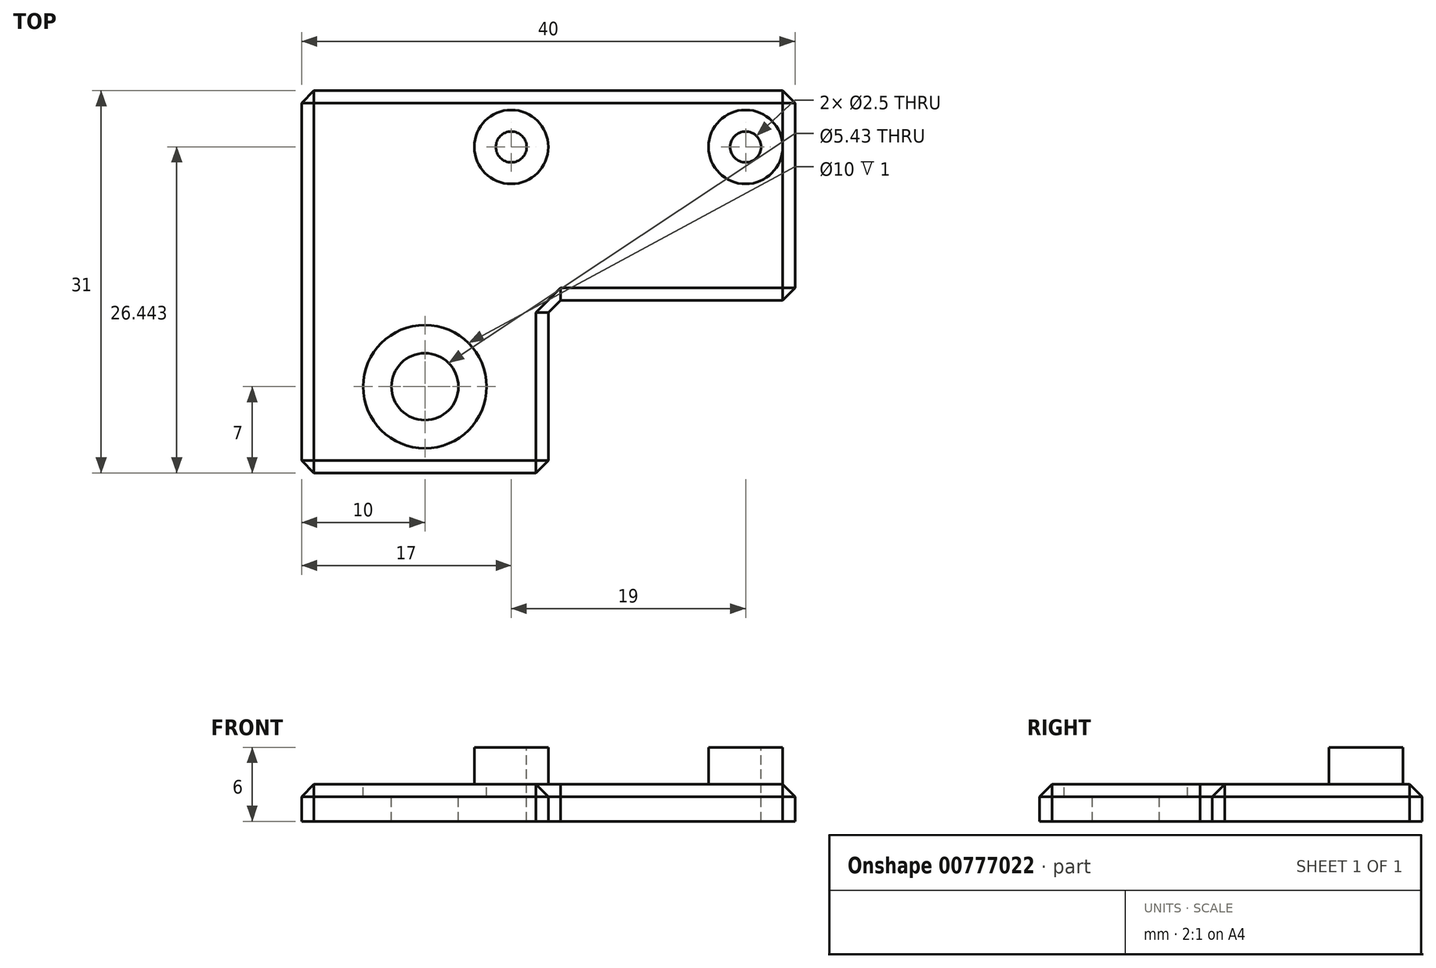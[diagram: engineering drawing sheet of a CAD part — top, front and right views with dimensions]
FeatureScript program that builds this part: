
annotation { "Feature Type Name" : "Feature", "Feature Type Description" : "" }
export const myFeature = defineFeature(function(context is Context, id is Id, definition is map)
    precondition{}
    {
        {
            var Q0;
            Q0=qCreatedBy(makeId("Top.planeOp"),FACE);
            var sketch = newSketch(context, id + "F0", { "sketchPlane" : qUnion([Q0])});
            skLineSegment(sketch, "E0.bottom", {"start": v(0, 0) * mm, "end": v(40, 0) * mm});
            skLineSegment(sketch, "E0.top", {"start": v(0, 17) * mm, "end": v(40, 17) * mm});
            skLineSegment(sketch, "E0.left", {"start": v(0, 0) * mm, "end": v(0, 17) * mm});
            skLineSegment(sketch, "E0.right", {"start": v(40, 0) * mm, "end": v(40, 17) * mm});
            skLineSegment(sketch, "E1", {"start": v(20, 29.26) * mm, "end": v(20, -19.83) * mm, "construction": true});
            skLineSegment(sketch, "E2.top", {"start": v(0, -14) * mm, "end": v(20, -14) * mm});
            skLineSegment(sketch, "E2.left", {"start": v(0, 0) * mm, "end": v(0, -14) * mm});
            skLineSegment(sketch, "E2.right", {"start": v(20, 0) * mm, "end": v(20, -14) * mm});
            skCircle(sketch, "E3", {"center": v(10, -7) * mm, "radius": 2.71 * mm});
            skCircle(sketch, "E4", {"center": v(17, 12.44) * mm, "radius": 1.25 * mm});
            skCircle(sketch, "E5", {"center": v(36, 12.44) * mm, "radius": 1.25 * mm});
            skCircle(sketch, "E6", {"center": v(17, 12.44) * mm, "radius": 3 * mm});
            skCircle(sketch, "E7", {"center": v(36, 12.44) * mm, "radius": 3 * mm});
            skSolve(sketch);
        }
        {
            var Q0;
            Q0=makeQuery(id+"F0.imprint","IMPRINT",FACE,{"disambiguationData":[TD([[makeQuery(id+"F0.imprint","IMPRINT",EDGE,{"derivedFrom":sQuery(id+"F0.wireOp",EDGE,"E2.top")}),1.0]])]});
            var Q1;
            Q1=makeQuery(id+"F0.imprint","IMPRINT",FACE,{"disambiguationData":[TD([[makeQuery(id+"F0.imprint","IMPRINT",EDGE,{"derivedFrom":sQuery(id+"F0.wireOp",EDGE,"E0.top")}),-1.0]])]});
            var Q2;
            Q2=makeQuery(id+"F0.imprint","IMPRINT",FACE,{"disambiguationData":[TD([[makeQuery(id+"F0.imprint","IMPRINT",EDGE,{"derivedFrom":sQuery(id+"F0.wireOp",EDGE,"E5")}),-1.0]])]});
            var Q3;
            Q3=makeQuery(id+"F0.imprint","IMPRINT",FACE,{"disambiguationData":[TD([[makeQuery(id+"F0.imprint","IMPRINT",EDGE,{"derivedFrom":sQuery(id+"F0.wireOp",EDGE,"E4")}),-1.0]])]});
            extrude(context, id + "F1", {"entities" : qUnion([Q0, Q1, Q2, Q3]), "oppositeDirection" : true, "depth" : 3 * mm, "offsetDistance" : 25 * mm});
        }
        {
            var Q0;
            Q0=makeQuery(id+"F1.opExtrude","CAP_FACE",FACE,{"disambiguationData":[OSD([sQuery(id+"F0.wireOp",EDGE,"E0.bottom"),sQuery(id+"F0.wireOp",EDGE,"E0.top"),sQuery(id+"F0.wireOp",EDGE,"E0.left"),sQuery(id+"F0.wireOp",EDGE,"E0.right"),sQuery(id+"F0.wireOp",EDGE,"E2.top"),sQuery(id+"F0.wireOp",EDGE,"E2.left"),sQuery(id+"F0.wireOp",EDGE,"E2.right"),sQuery(id+"F0.wireOp",EDGE,"hfNWk83l-vukS-OY9w-RtWu-MQcwIE22JMWj"),sQuery(id+"F0.wireOp",EDGE,"E4"),sQuery(id+"F0.wireOp",EDGE,"E5")])],"isStart":true});
            var sketch = newSketch(context, id + "F2", { "sketchPlane" : qUnion([Q0])});
            skCircle(sketch, "E8", {"center": v(10, -7) * mm, "radius": 5 * mm});
            skSolve(sketch);
        }
        {
            var Q0;
            Q0=makeQuery(id+"F2.imprint","IMPRINT",FACE,{"disambiguationData":[TD([[makeQuery(id+"F2.imprint","IMPRINT",EDGE,{"derivedFrom":sQuery(id+"F2.wireOp",EDGE,"E8")}),1.0]])]});
            extrude(context, id + "F3", {"entities" : qUnion([Q0]), "operationType" : NewBodyOperationType.REMOVE, "oppositeDirection" : true, "depth" : 1 * mm, "offsetDistance" : 25 * mm});
        }
        {
            var Q0;
            Q0=makeQuery(id+"F0.imprint","IMPRINT",FACE,{"disambiguationData":[TD([[makeQuery(id+"F0.imprint","IMPRINT",EDGE,{"derivedFrom":sQuery(id+"F0.wireOp",EDGE,"E4")}),-1.0]])]});
            var Q1;
            Q1=makeQuery(id+"F0.imprint","IMPRINT",FACE,{"disambiguationData":[TD([[makeQuery(id+"F0.imprint","IMPRINT",EDGE,{"derivedFrom":sQuery(id+"F0.wireOp",EDGE,"E5")}),-1.0]])]});
            extrude(context, id + "F4", {"entities" : qUnion([Q0, Q1]), "operationType" : NewBodyOperationType.ADD, "depth" : 3 * mm, "offsetDistance" : 25 * mm});
        }
        {
            var Q0;
            Q0=makeQuery(id+"F1.opExtrude","CAP_EDGE",EDGE,{"disambiguationData":[OSD([sQuery(id+"F0.wireOp",EDGE,"E0.left"),sQuery(id+"F0.wireOp",EDGE,"E2.left")])],"isStart":true});
            var Q1;
            Q1=makeQuery(id+"F1.opExtrude","CAP_EDGE",EDGE,{"disambiguationData":[OSD([sQuery(id+"F0.wireOp",EDGE,"E2.top")])],"isStart":true});
            var Q2;
            Q2=makeQuery(id+"F1.opExtrude","CAP_EDGE",EDGE,{"disambiguationData":[OSD([sQuery(id+"F0.wireOp",EDGE,"E2.right")])],"isStart":true});
            var Q3;
            Q3=makeQuery(id+"F1.opExtrude","CAP_EDGE",EDGE,{"disambiguationData":[OSD([sQuery(id+"F0.wireOp",EDGE,"E0.bottom")])],"isStart":true});
            var Q4;
            Q4=makeQuery(id+"F1.opExtrude","CAP_EDGE",EDGE,{"disambiguationData":[OSD([sQuery(id+"F0.wireOp",EDGE,"E0.right")])],"isStart":true});
            var Q5;
            Q5=makeQuery(id+"F1.opExtrude","CAP_EDGE",EDGE,{"disambiguationData":[OSD([sQuery(id+"F0.wireOp",EDGE,"E0.top")])],"isStart":true});
            var Q6;
            Q6=makeQuery(id+"F1.opExtrude","SWEPT_EDGE",EDGE,{"disambiguationData":[OSD([sQuery(id+"F0.wireOp",EDGE,"E0.bottom"),sQuery(id+"F0.wireOp",EDGE,"E0.right")])]});
            var Q7;
            Q7=makeQuery(id+"F1.opExtrude","SWEPT_EDGE",EDGE,{"disambiguationData":[OSD([sQuery(id+"F0.wireOp",EDGE,"E0.top"),sQuery(id+"F0.wireOp",EDGE,"E0.right")])]});
            var Q8;
            Q8=makeQuery(id+"F1.opExtrude","SWEPT_EDGE",EDGE,{"disambiguationData":[OSD([sQuery(id+"F0.wireOp",EDGE,"E2.top"),sQuery(id+"F0.wireOp",EDGE,"E2.right")])]});
            var Q9;
            Q9=makeQuery(id+"F1.opExtrude","SWEPT_EDGE",EDGE,{"disambiguationData":[OSD([sQuery(id+"F0.wireOp",EDGE,"E0.top"),sQuery(id+"F0.wireOp",EDGE,"E0.left")])]});
            var Q10;
            Q10=makeQuery(id+"F1.opExtrude","SWEPT_EDGE",EDGE,{"disambiguationData":[OSD([sQuery(id+"F0.wireOp",EDGE,"E2.top"),sQuery(id+"F0.wireOp",EDGE,"E2.left")])]});
            var Q11;
            Q11=makeQuery(id+"F1.opExtrude","SWEPT_EDGE",EDGE,{"disambiguationData":[OSD([sQuery(id+"F0.wireOp",EDGE,"E0.bottom"),sQuery(id+"F0.wireOp",EDGE,"E2.right")])]});
            chamfer(context, id + "F5", {"entities" : qUnion([Q0, Q1, Q2, Q3, Q4, Q5, Q6, Q7, Q8, Q9, Q10, Q11]), "width" : 1 * mm, "tangentPropagation" : true});
        }
    });
